# Revit family: IS_iLifeB_T5336_BIM_GB
name_source: partatom
category: Plumbing Fixtures
units: mm (PartAtom-declared; Revit-internal decimal feet)

## family parameters
Always vertical = No
Cut with Voids When Loaded = No
OmniClass Number = 23.45.05.14.14
OmniClass Title = Sinks/Lavatories
Part Type = Normal
Room Calculation Point = No
Round Connector Dimension = Use Diameter
Shared = No
Work Plane-Based = No

## types (2) — shared parameters
Accessories = https://www.idealstandard.co.uk
AreaMeasurement = Internal
AreaUnits = Millimetres
BIMObjectName = IS_IdealStandard_Wall-hungwashbasins_i.lifeB_T5336
BIMobject category = Wash Basins
BIMobject category code = wash-basins
BIMobject main category = Sanitary
BIMobject main category code = sanitary
Brand url = http://www.idealstandard.co.uk
Category = Sanitary
Classification = Washbasin
ConnectionType = Plumbing
CurrencyUnit = £
CurrentRevision = 1
Date of publishing = 22/07/2022
DurationUnit = Years
Edition number = 1
ElementType = Fixed
ExpectedLife = 99
GTIN code = https://8014140503798
Help = https://www.idealstandard.co.uk
IFC Classification = Sanitary Terminal
IfcExportAs = IfcSanitaryTerminalType
IfcExportType = WASHHANDBASIN
Installation instructions = https://www.idealstandard.co.uk
InstallationInstructions = https://www.idealstandard.co.uk
LinearUnits = millimitres
MaintenanceInformation = https://www.idealstandard.co.uk
Manufacturer = Ideal Standard
Manufacturer name = Ideal Standard
ManufacturerURL = https://www.idealstandard.co.uk
Material = Fireclay
Material main = Fireclay
ModelReference = Ideal Standard i.life B  basin 55 cm without taphole and with overflow
NBS Reference Code = 45-35-70/368
NBS Reference Description = Wall hung hand rinse basins
Name = Wall-hungwashbasins_i.lifeB_T5336_IdealStandard
NominalDepth = 440 mm
NominalHeight = 180 mm
NominalLength = 440 mm
NominalWidth = 549 mm
OmniClass Code = 23-39 29 13 21 19
OmniClass Description = Surface Water Retention Basins
PredefinedType = Washbasin
Product Guid = 10e5f1d4-675f-4064-b6e4-eb4c648241d1
Product SKU = T5336
Product certification = https://www.idealstandard.co.uk
Product data url = https://bimobject.com
Product family = Washbasin
Product group = Sanitary
Product name = I.Life b basin 55 cm without taphole
Product url = https://www.idealstandard.co.uk
ProductInformation = https://www.idealstandard.co.uk
QR code = http://bimobject.com
Shape = Sculptured
Size = 550 x 440 x 180 mm
Space = Internal
SpareParts = https://www.idealstandard.co.uk
Technical description = https://www.idealstandard.co.uk
UNSPSC Code = 301815
URL = https://www.idealstandard.co.uk
Uniclass 2015 Code = Pr_40_20_96_96
Uniclass 2015 Name = Wall-hung washbasins
Uniclass2015Code = Pr_40_20_96_96
Uniclass2015Title = Wall-hung washbasins
Uniclass2015Version = v1.25
Version = 1
VolumeUnits = Liters
WRASURL = https://www.wrasapprovals.co.uk
WarrantyDescription = manufacturer warranty
WarrantyDurationUnit = years
WashHandBasinMounting = Wall hung
WashHandBasinType = Wall Hung washbasin
Youtube clip = https://www.youtube.com

## per-type parameters (varying)
| type | BarCode | Color | Description | Features | Finish | MainColor | Model | ModelNumber | NettWeight | Weight Net (Kg) |
| T533601 - Ideal Standard i.life B  basin 55 cm without taphole and with overflow - White Finish | 8014140503798 | White | Ideal Standard i.life B  basin 55 cm without taphole, with overflow, white, in carton box, EU pallet | basin 55 cm without taphole, with overflow, white, in carton box, EU pallet | White | White | T533601 | T533601 | 15.3 | 44 |
| T5336MA - Ideal Standard i.life B  basin 55 cm without taphole and with overflow  - Ideal Plus White | 8014140509486 | Ideal Plus White | Ideal Standard i.life B  basin 55 cm without taphole, with overflow, white Ideal Plus, in carton box, EU pallet | basin 55 cm without taphole, with overflow, white Ideal Plus, in carton box, EU pallet | Ideal Plus White | Ideal Plus White | T5336MA | T5336MA | 17.82 | 48 |

## geometry (parser evidence)
native form markers: Sweep x2
no freeform markers — native parametric forms only
